# Revit family: Holdown-Simpson_Strong_Tie-LSTHD_STHD-3D
name_source: partatom
category: Structural Connections
revit_build: Autodesk Revit Structure 2012 (Build: 20110309_2315(x64)
units: mm (PartAtom-declared; Revit-internal decimal feet)

## types (1)
- Use Type Catalog
    Code Reference = Use Type Catalog
    DF/SP/SPF/HF_Allowable Loads_Tension_Cracked_Corner = Use Type Catalog
    DF/SP/SPF/HF_Allowable Loads_Tension_Cracked_Endwall = Use Type Catalog
    DF/SP/SPF/HF_Allowable Loads_Tension_Cracked_Midwall = Use Type Catalog
    DF/SP/SPF/HF_Allowable Loads_Tension_Non Cracked_Corner = Use Type Catalog
    DF/SP/SPF/HF_Allowable Loads_Tension_Non Cracked_Endwall = Use Type Catalog
    DF/SP/SPF/HF_Allowable Loads_Tension_Non Cracked_Midwall = Use Type Catalog
    Date Last Modified = May 09 2013
    Default Elevation = 0"
    Description = Holdowns
    Embedment Length = 8"
    Embedment Length Control = 2 27/32"
    Equipment Abbreviation = Use Type Catalog
    Family Version = 1.0.0
    Fasteners_Quantity = 0
    Fasteners_Type = Use Type Catalog
    Is Void = Yes
    Length = 18 5/8"
    Manufacturer = Simpson Strong-Tie Company Inc.
    Metal Gauge = 0
    Min. Stem Wall = 0"
    Model = Use Type Catalog
    Model Disclaimer = Contact Simpson Strong-Tie Company Inc. for more information
    Model ID = F7CC5208-CDF1-46B8-9A7E-B7E843668332
    Part Description = Holdowns
    Part Number = Use Type Catalog
    Product Documentation Link = http://www.strongtie.com
    Product Material = Steel - Simpson - Galvanized
    Provide Feedback = http://www.strongtie.com
    Type Comments = Holdowns
    URL = http://www.strongtie.com
    Width = 3"

## geometry (parser evidence)
native form markers: Blend x1, Sweep x3
no freeform markers — native parametric forms only
